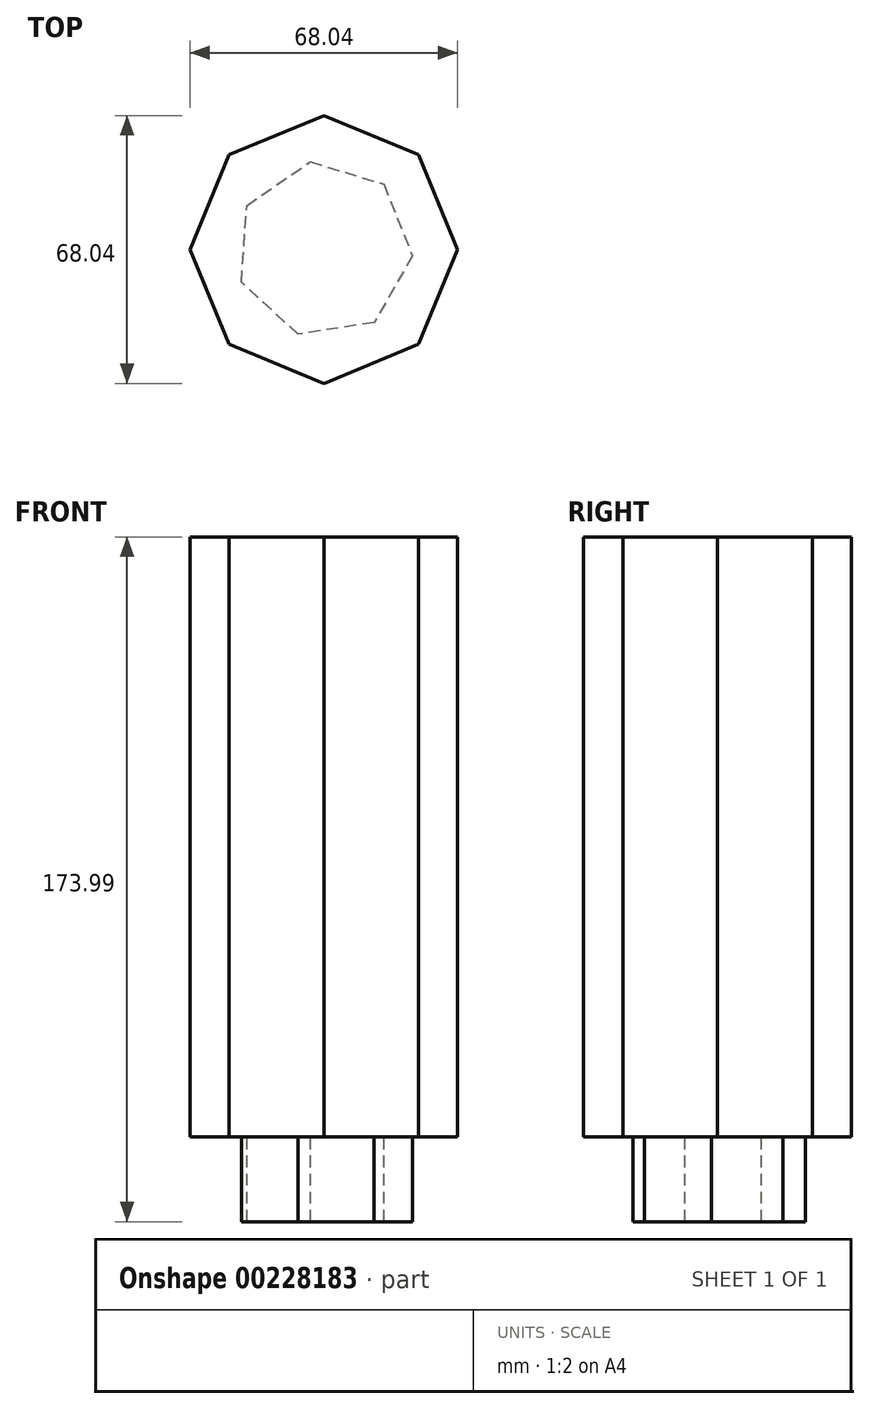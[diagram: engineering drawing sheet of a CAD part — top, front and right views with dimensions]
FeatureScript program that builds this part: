
annotation { "Feature Type Name" : "Feature", "Feature Type Description" : "" }
export const myFeature = defineFeature(function(context is Context, id is Id, definition is map)
    precondition{}
    {
        {
            var Q0;
            Q0=qCreatedBy(makeId("Top.planeOp"),FACE);
            var sketch = newSketch(context, id + "F0", { "sketchPlane" : qUnion([Q0])});
            skCircle(sketch, "E0.cCircle", {"center": v(0, 0) * mm, "radius": 34.02 * mm, "construction": true});
            skLineSegment(sketch, "E0.0", {"start": v(34.02, 0) * mm, "end": v(24.06, -24.06) * mm});
            skLineSegment(sketch, "E0.1", {"start": v(24.06, -24.06) * mm, "end": v(0, -34.02) * mm});
            skLineSegment(sketch, "E0.2", {"start": v(0, -34.02) * mm, "end": v(-24.06, -24.06) * mm});
            skLineSegment(sketch, "E0.3", {"start": v(-24.06, -24.06) * mm, "end": v(-34.02, 0) * mm});
            skLineSegment(sketch, "E0.4", {"start": v(-34.02, 0) * mm, "end": v(-24.06, 24.06) * mm});
            skLineSegment(sketch, "E0.5", {"start": v(-24.06, 24.06) * mm, "end": v(0, 34.02) * mm});
            skLineSegment(sketch, "E0.6", {"start": v(0, 34.02) * mm, "end": v(24.06, 24.06) * mm});
            skLineSegment(sketch, "E0.7", {"start": v(24.06, 24.06) * mm, "end": v(34.02, 0) * mm});
            skSolve(sketch);
        }
        {
            var Q0;
            Q0=makeQuery(id+"F0.imprint","IMPRINT",FACE,{"disambiguationData":[TD([[makeQuery(id+"F0.imprint","IMPRINT",EDGE,{"derivedFrom":sQuery(id+"F0.wireOp",EDGE,"E0.0")}),-1.0]])]});
            extrude(context, id + "F1", {"entities" : qUnion([Q0]), "depth" : 152.4 * mm, "hasDraft" : true, "draftAngle" : 0 * degree});
        }
        {
            var Q0;
            Q0=makeQuery(id+"F1.opExtrude","CAP_FACE",FACE,{"disambiguationData":[OSD([sQuery(id+"F0.wireOp",EDGE,"E0.0"),sQuery(id+"F0.wireOp",EDGE,"E0.1"),sQuery(id+"F0.wireOp",EDGE,"E0.2"),sQuery(id+"F0.wireOp",EDGE,"E0.3"),sQuery(id+"F0.wireOp",EDGE,"E0.4"),sQuery(id+"F0.wireOp",EDGE,"E0.5"),sQuery(id+"F0.wireOp",EDGE,"E0.6"),sQuery(id+"F0.wireOp",EDGE,"E0.7")])],"isStart":false});
            var sketch = newSketch(context, id + "F2", { "sketchPlane" : qUnion([Q0])});
            skCircle(sketch, "E1.cCircle", {"center": v(0, 0) * mm, "radius": 22.53 * mm, "construction": true});
            skLineSegment(sketch, "E1.0", {"start": v(-19.55, 11.2) * mm, "end": v(-3.44, 22.27) * mm});
            skLineSegment(sketch, "E1.1", {"start": v(-3.44, 22.27) * mm, "end": v(15.26, 16.57) * mm});
            skLineSegment(sketch, "E1.2", {"start": v(15.26, 16.57) * mm, "end": v(22.47, -1.6) * mm});
            skLineSegment(sketch, "E1.3", {"start": v(22.47, -1.6) * mm, "end": v(12.76, -18.57) * mm});
            skLineSegment(sketch, "E1.4", {"start": v(12.76, -18.57) * mm, "end": v(-6.56, -21.55) * mm});
            skLineSegment(sketch, "E1.5", {"start": v(-6.56, -21.55) * mm, "end": v(-20.94, -8.3) * mm});
            skLineSegment(sketch, "E1.6", {"start": v(-20.94, -8.3) * mm, "end": v(-19.55, 11.2) * mm});
            skSolve(sketch);
        }
        {
            var Q0;
            Q0=makeQuery(id+"F2.imprint","IMPRINT",FACE,{"disambiguationData":[TD([[makeQuery(id+"F2.imprint","IMPRINT",EDGE,{"derivedFrom":sQuery(id+"F2.wireOp",EDGE,"E1.0")}),-1.0]])]});
            extrude(context, id + "F3", {"entities" : qUnion([Q0]), "operationType" : NewBodyOperationType.ADD, "oppositeDirection" : true, "depth" : 174 * mm});
        }
    });
